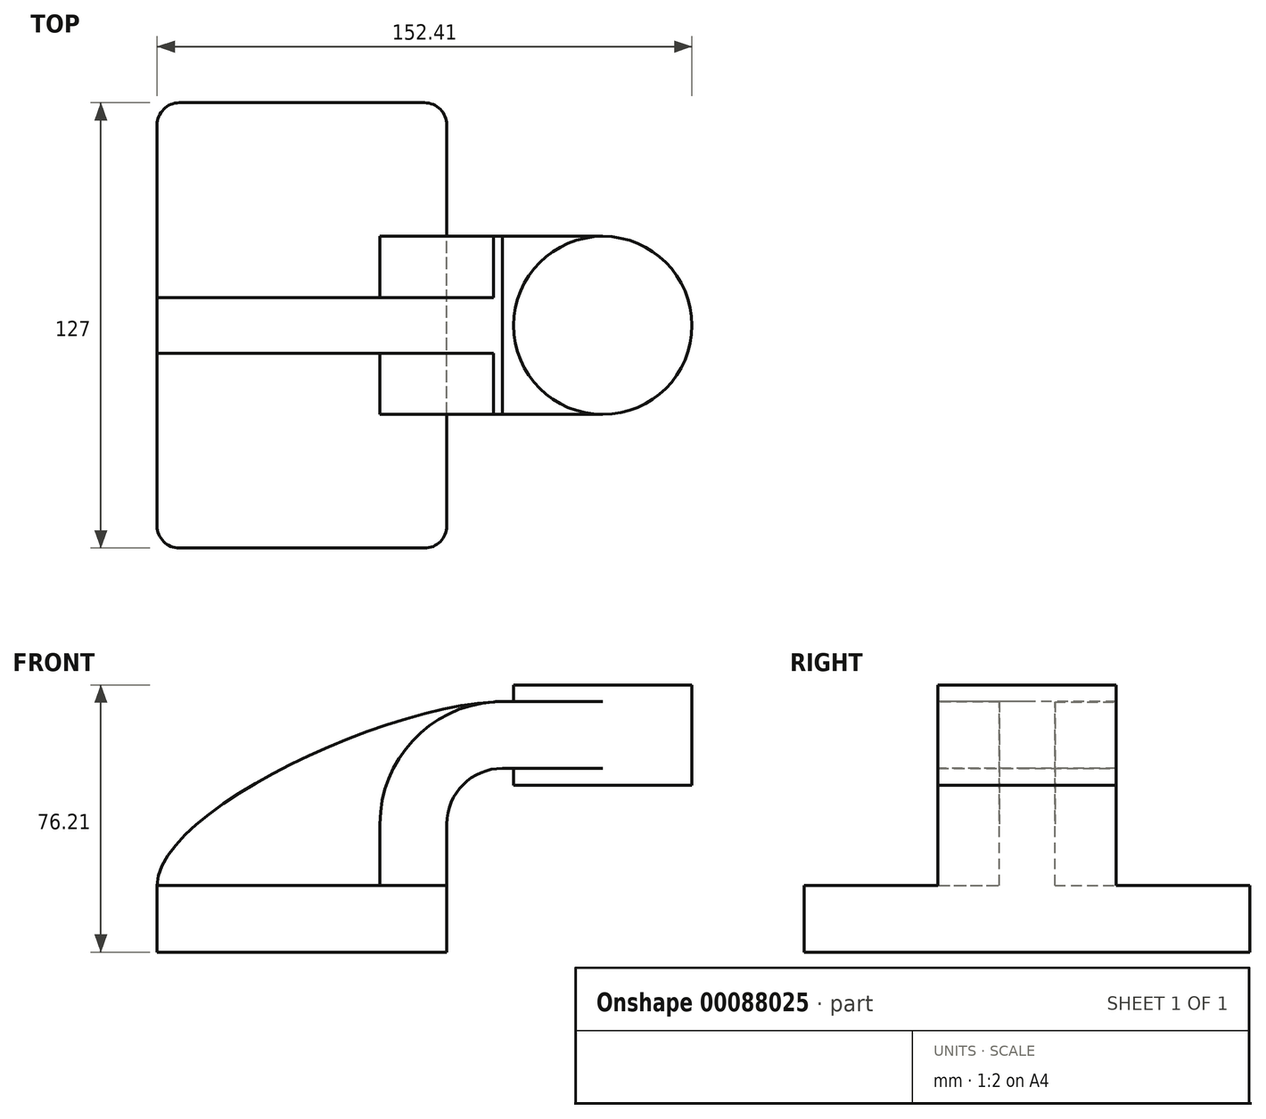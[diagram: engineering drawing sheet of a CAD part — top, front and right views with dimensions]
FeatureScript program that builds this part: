
annotation { "Feature Type Name" : "Feature", "Feature Type Description" : "" }
export const myFeature = defineFeature(function(context is Context, id is Id, definition is map)
    precondition{}
    {
        {
            var Q0;
            Q0=qCreatedBy(makeId("Front.planeOp"),FACE);
            var sketch = newSketch(context, id + "F0", { "sketchPlane" : qUnion([Q0])});
            skLineSegment(sketch, "E0.bottom", {"start": v(41.27, 9.53) * mm, "end": v(-41.28, 9.53) * mm});
            skLineSegment(sketch, "E0.top", {"start": v(41.28, -9.52) * mm, "end": v(-41.27, -9.52) * mm});
            skLineSegment(sketch, "E0.left", {"start": v(41.28, 9.53) * mm, "end": v(41.28, -9.52) * mm});
            skLineSegment(sketch, "E0.right", {"start": v(-41.28, 9.53) * mm, "end": v(-41.27, -9.52) * mm});
            skPoint(sketch, "E0.middle", {"position": v(0, 0) * mm});
            skLineSegment(sketch, "E1.bottom", {"start": v(60.32, 38.1) * mm, "end": v(111.12, 38.1) * mm});
            skLineSegment(sketch, "E1.top", {"start": v(60.32, 66.68) * mm, "end": v(111.12, 66.68) * mm});
            skLineSegment(sketch, "E1.left", {"start": v(60.32, 38.1) * mm, "end": v(60.32, 66.68) * mm});
            skLineSegment(sketch, "E1.right", {"start": v(111.12, 38.1) * mm, "end": v(111.12, 66.68) * mm});
            skPoint(sketch, "E1.middle", {"position": v(85.72, 52.39) * mm});
            skLineSegment(sketch, "E2", {"start": v(41.27, 9.53) * mm, "end": v(41.27, 27) * mm});
            skArc(sketch, "E3", {"start": v(41.28, 27) * mm, "mid": v(45.92, 38.23) * mm, "end": v(57.15, 42.88) * mm});
            skLineSegment(sketch, "E4", {"start": v(57.15, 42.88) * mm, "end": v(85.72, 42.88) * mm});
            skLineSegment(sketch, "E5", {"start": v(85.72, 38.1) * mm, "end": v(85.72, 66.68) * mm});
            skLineSegment(sketch, "E6.0", {"start": v(57.15, 61.93) * mm, "end": v(85.72, 61.93) * mm});
            skArc(sketch, "E6.1", {"start": v(22.23, 27) * mm, "mid": v(32.45, 51.7) * mm, "end": v(57.15, 61.93) * mm});
            skLineSegment(sketch, "E6.2", {"start": v(22.22, 9.53) * mm, "end": v(22.22, 27) * mm});
            skFitSpline(sketch, "E7", {"points": [v(-41.28, 9.53) * mm, v(57.15, 61.93) * mm], "startDerivative": vector(0.45, 63.42) * mm, "endDerivative": vector(98, 1.37) * mm});
            skSolve(sketch);
        }
        {
            var Q0;
            Q0=makeQuery(id+"F0.imprint","IMPRINT",FACE,{"disambiguationData":[TD([[makeQuery(id+"F0.imprint","IMPRINT",EDGE,{"derivedFrom":sQuery(id+"F0.wireOp",EDGE,"E0.top")}),-1.0]])]});
            extrude(context, id + "F1", {"entities" : qUnion([Q0]), "endBound" : BoundingType.SYMMETRIC, "depth" : 127 * mm});
        }
        {
            var Q0;
            {var subQ1=sQuery(id+"F0.wireOp",EDGE,"E2");Q0=makeQuery(id+"F0.imprint","IMPRINT",FACE,{"disambiguationData":[TD([[makeQuery(id+"F0.imprint","IMPRINT",EDGE,{"derivedFrom":subQ1}),1.0]])]});}
            var Q1;
            {var subQ0=sQuery(id+"F0.wireOp",EDGE,"E4");var subQ1=sQuery(id+"F0.wireOp",EDGE,"E1.left");var subQ2=makeQuery(id+"F0.imprint","INTERSECT",VERTEX,{"derivedFrom":[subQ1,subQ0]});Q1=makeQuery(id+"F0.imprint","IMPRINT",FACE,{"disambiguationData":[TD([[makeQuery(id+"F0.imprint","IMPRINT",EDGE,{"disambiguationData":[TD([[subQ2,-1.0]])],"derivedFrom":subQ1}),-1.0]])]});}
            extrude(context, id + "F2", {"entities" : qUnion([Q0, Q1]), "operationType" : NewBodyOperationType.ADD, "endBound" : BoundingType.SYMMETRIC, "depth" : 50.8 * mm});
        }
        {
            var Q0;
            {var subQ3=sQuery(id+"F0.wireOp",EDGE,"E6.2");Q0=makeQuery(id+"F0.imprint","IMPRINT",FACE,{"disambiguationData":[TD([[makeQuery(id+"F0.imprint","IMPRINT",EDGE,{"derivedFrom":subQ3}),1.0]])]});}
            extrude(context, id + "F3", {"entities" : qUnion([Q0]), "operationType" : NewBodyOperationType.ADD, "endBound" : BoundingType.SYMMETRIC, "depth" : 15.88 * mm});
        }
        {
            var Q0;
            {var subQ4=sQuery(id+"F0.wireOp",EDGE,"E1.right");Q0=makeQuery(id+"F0.imprint","IMPRINT",FACE,{"disambiguationData":[TD([[makeQuery(id+"F0.imprint","IMPRINT",EDGE,{"derivedFrom":subQ4}),1.0]])]});}
            var Q1;
            Q1=sQuery(id+"F0.wireOp",EDGE,"E5");
            revolve(context, id + "F4", {"operationType" : NewBodyOperationType.ADD, "entities" : qUnion([Q0]), "axis" : qUnion([Q1]), "revolveType" : RevolveType.FULL});
        }
        {
            var Q0;
            Q0=makeQuery(id+"F1.opExtrude","CAP_EDGE",EDGE,{"disambiguationData":[OSD([sQuery(id+"F0.wireOp",EDGE,"E0.right")])],"isStart":false});
            var Q1;
            Q1=makeQuery(id+"F1.opExtrude","CAP_EDGE",EDGE,{"disambiguationData":[OSD([sQuery(id+"F0.wireOp",EDGE,"E0.left")])],"isStart":false});
            var Q2;
            Q2=makeQuery(id+"F1.opExtrude","CAP_EDGE",EDGE,{"disambiguationData":[OSD([sQuery(id+"F0.wireOp",EDGE,"E0.left")])],"isStart":true});
            var Q3;
            Q3=makeQuery(id+"F1.opExtrude","CAP_EDGE",EDGE,{"disambiguationData":[OSD([sQuery(id+"F0.wireOp",EDGE,"E0.right")])],"isStart":true});
            fillet(context, id + "F5", {"entities" : qUnion([Q0, Q1, Q2, Q3]), "radius" : 6.35 * mm, "tangentPropagation" : true, "allowEdgeOverflow" : false});
        }
    });
